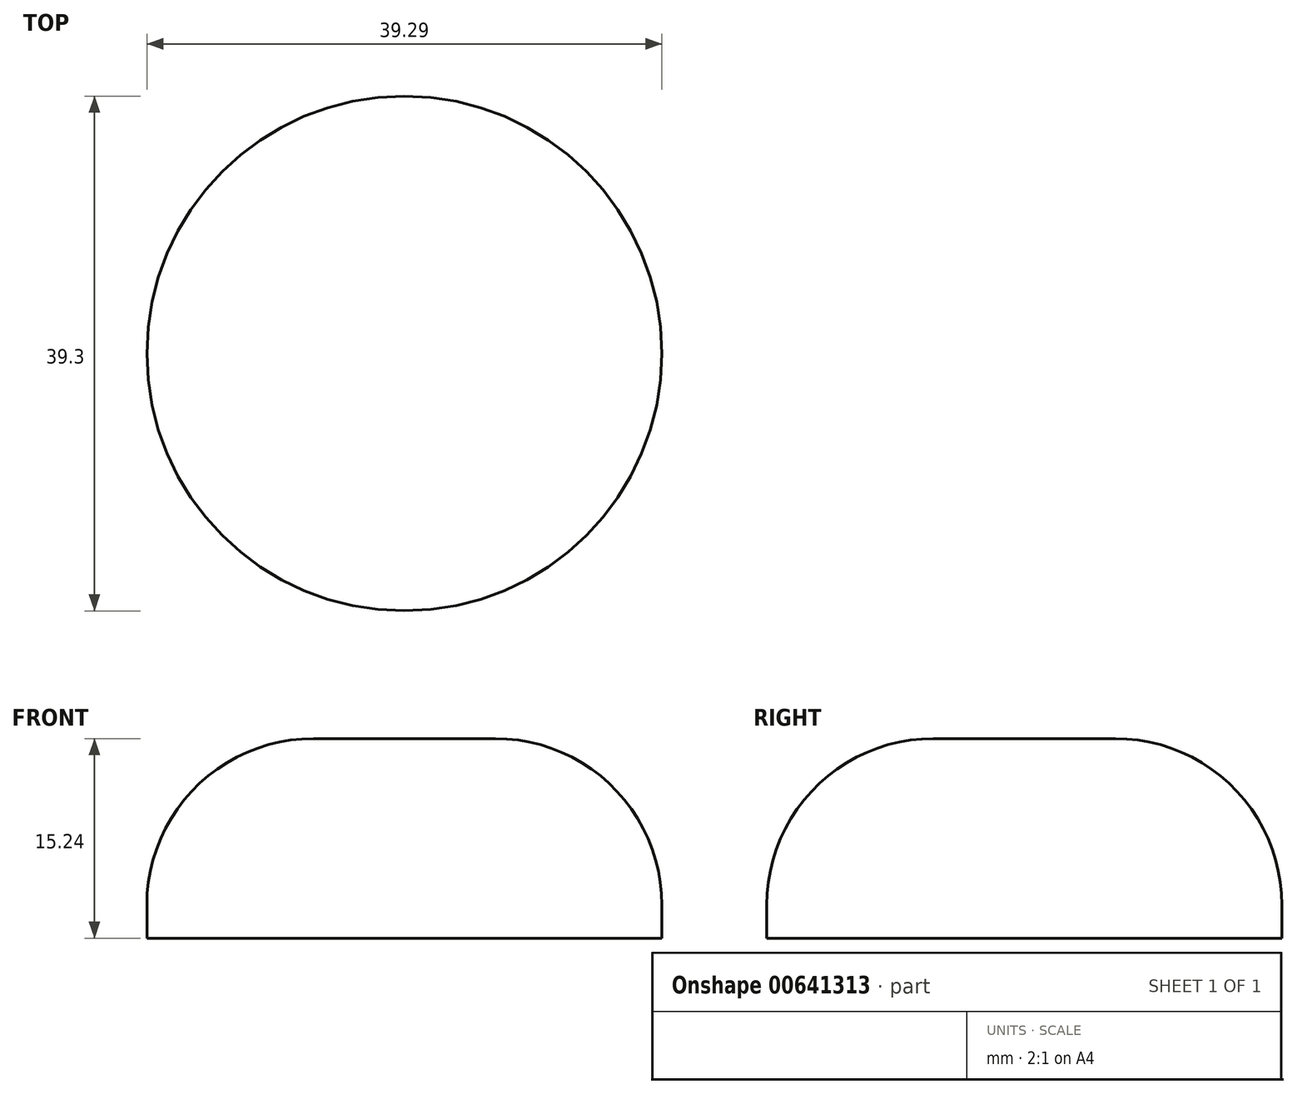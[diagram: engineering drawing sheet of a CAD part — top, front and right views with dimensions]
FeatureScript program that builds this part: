
annotation { "Feature Type Name" : "Feature", "Feature Type Description" : "" }
export const myFeature = defineFeature(function(context is Context, id is Id, definition is map)
    precondition{}
    {
        {
            var Q0;
            Q0=qCreatedBy(makeId("Top.planeOp"),FACE);
            var sketch = newSketch(context, id + "F0", { "sketchPlane" : qUnion([Q0])});
            skCircle(sketch, "E0", {"center": v(35.94, 0) * mm, "radius": 19.65 * mm});
            skLineSegment(sketch, "E1", {"start": v(20.16, 11.7) * mm, "end": v(-33.84, 11.7) * mm});
            skLineSegment(sketch, "E2", {"start": v(-33.84, 11.7) * mm, "end": v(-33.84, -11.58) * mm});
            skLineSegment(sketch, "E3", {"start": v(-33.84, -11.58) * mm, "end": v(20.07, -11.58) * mm});
            skSolve(sketch);
        }
        {
            var Q0;
            {var subQ0=sQuery(id+"F0.wireOp",EDGE,"E0");var subQ1=makeQuery(id+"F0.imprint","INTERSECT",VERTEX,{"derivedFrom":[subQ0,sQuery(id+"F0.wireOp",EDGE,"E1")]});Q0=makeQuery(id+"F0.imprint","IMPRINT",FACE,{"disambiguationData":[TD([[makeQuery(id+"F0.imprint","IMPRINT",EDGE,{"disambiguationData":[TD([[subQ1,-1.0]])],"derivedFrom":subQ0}),1.0]])]});}
            extrude(context, id + "F1", {"entities" : qUnion([Q0]), "depth" : 15.24 * mm, "offsetDistance" : 25.4 * mm});
        }
        {
            var Q0;
            Q0=makeQuery(id+"F1.opExtrude","CAP_FACE",FACE,{"disambiguationData":[OSD([sQuery(id+"F0.wireOp",EDGE,"E0")])],"isStart":false});
            fillet(context, id + "F2", {"entities" : qUnion([Q0]), "radius" : 12.7 * mm, "tangentPropagation" : true, "allowEdgeOverflow" : false});
        }
    });
